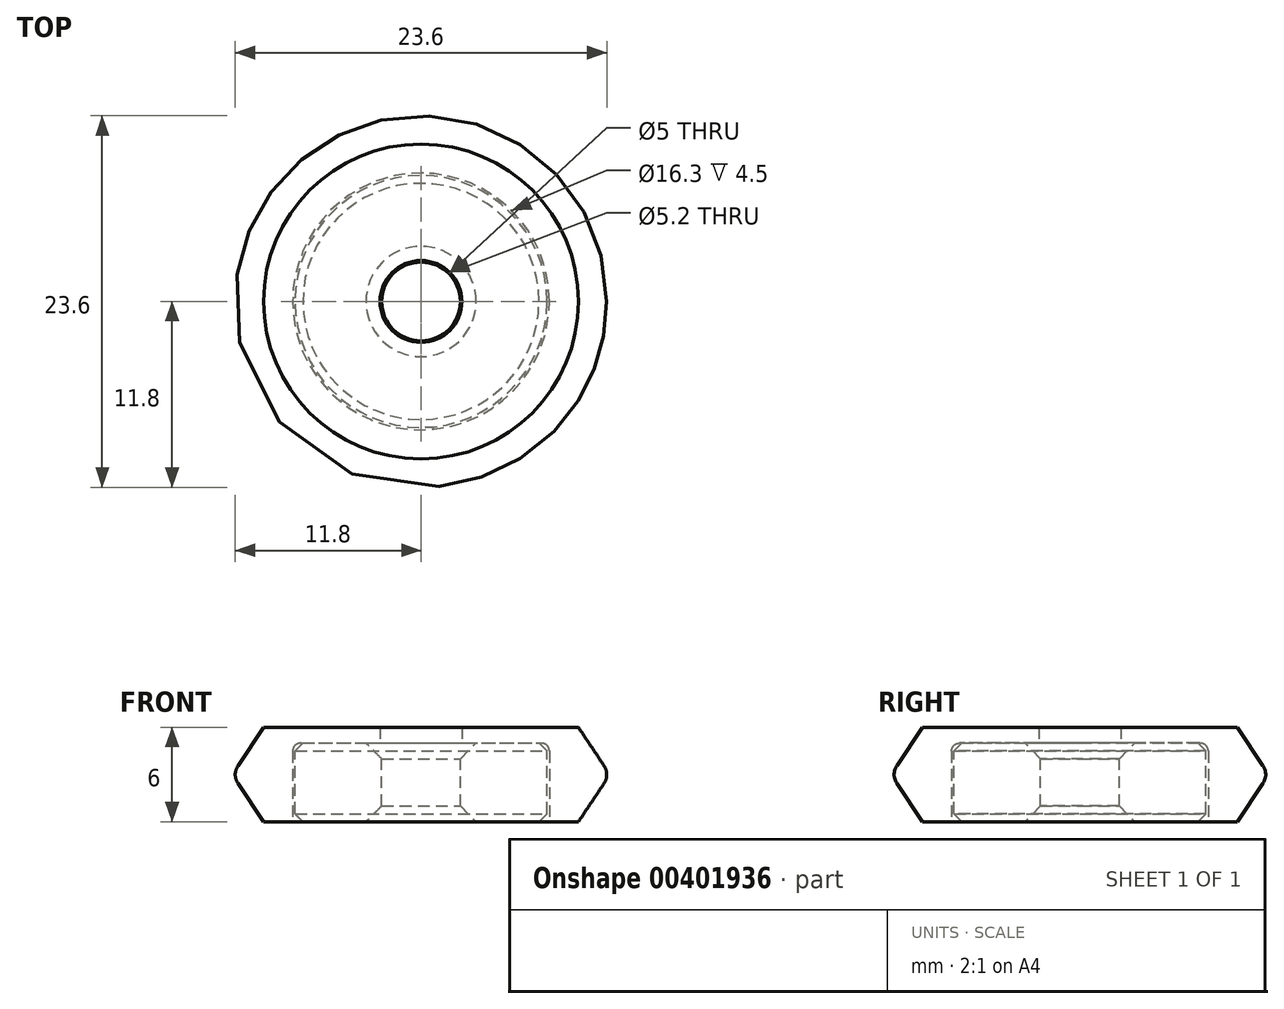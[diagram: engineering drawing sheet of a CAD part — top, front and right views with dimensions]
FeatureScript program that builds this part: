
annotation { "Feature Type Name" : "Feature", "Feature Type Description" : "" }
export const myFeature = defineFeature(function(context is Context, id is Id, definition is map)
    precondition{}
    {
        {
            var Q0;
            Q0=qCreatedBy(makeId("Top.planeOp"),FACE);
            var sketch = newSketch(context, id + "F0", { "sketchPlane" : qUnion([Q0])});
            skCircle(sketch, "E0", {"center": v(0, 0) * mm, "radius": 10 * mm});
            skSolve(sketch);
        }
        {
            var Q0;
            Q0=qCreatedBy(makeId("Top.planeOp"),FACE);
            cPlane(context, id + "F1", {"entities" : qUnion([Q0]), "cplaneType" : CPlaneType.OFFSET, "offset" : 3 * mm, "width" : 150 * mm, "height" : 150 * mm});
        }
        {
            var Q0;
            Q0=qCreatedBy(id+"F1.planeOp",FACE);
            var sketch = newSketch(context, id + "F2", { "sketchPlane" : qUnion([Q0])});
            skCircle(sketch, "E1", {"center": v(0, 0) * mm, "radius": 12 * mm});
            skSolve(sketch);
        }
        {
            var Q0;
            Q0=makeQuery(id+"F2.imprint","IMPRINT",FACE,{"disambiguationData":[TD([[makeQuery(id+"F2.imprint","IMPRINT",EDGE,{"derivedFrom":sQuery(id+"F2.wireOp",EDGE,"E1")}),1.0]])]});
            var Q1;
            Q1=makeQuery(id+"F0.imprint","IMPRINT",FACE,{"disambiguationData":[TD([[makeQuery(id+"F0.imprint","IMPRINT",EDGE,{"derivedFrom":sQuery(id+"F0.wireOp",EDGE,"E0")}),1.0]])]});
            loft(context, id + "F3", {"sheetProfilesArray" : [{ "sheetProfileEntities" : qUnion([Q0]) }, { "sheetProfileEntities" : qUnion([Q1]) }]});
        }
        {
            var Q0;
            Q0=makeQuery(id+"F3.opLoft","SWEPT_BODY",BODY,{"disambiguationData":[OSD([makeQuery(id+"F0.imprint","IMPRINT",FACE,{"disambiguationData":[TD([[makeQuery(id+"F0.imprint","IMPRINT",EDGE,{"derivedFrom":sQuery(id+"F0.wireOp",EDGE,"E0")}),1.0]])]}),makeQuery(id+"F2.imprint","IMPRINT",FACE,{"disambiguationData":[TD([[makeQuery(id+"F2.imprint","IMPRINT",EDGE,{"derivedFrom":sQuery(id+"F2.wireOp",EDGE,"E1")}),1.0]])]})])]});
            var Q1;
            Q1=qCreatedBy(id+"F1.planeOp",FACE);
            mirror(context, id + "F4", {"operationType" : NewBodyOperationType.ADD, "entities" : qUnion([Q0]), "mirrorPlane" : qUnion([Q1])});
        }
        {
            var Q0;
            Q0=makeQuery(id+"F3.opLoft","CAP_FACE",FACE,{"disambiguationData":[OSD([makeQuery(id+"F0.imprint","IMPRINT",FACE,{"disambiguationData":[TD([[makeQuery(id+"F0.imprint","IMPRINT",EDGE,{"derivedFrom":sQuery(id+"F0.wireOp",EDGE,"E0")}),1.0]])]})])],"isStart":true});
            var sketch = newSketch(context, id + "F5", { "sketchPlane" : qUnion([Q0])});
            skCircle(sketch, "E2", {"center": v(0, 0) * mm, "radius": 8.15 * mm});
            skSolve(sketch);
        }
        {
            var Q0;
            Q0=makeQuery(id+"F5.imprint","IMPRINT",FACE,{"disambiguationData":[TD([[makeQuery(id+"F5.imprint","IMPRINT",EDGE,{"derivedFrom":sQuery(id+"F5.wireOp",EDGE,"E2")}),1.0]])]});
            extrude(context, id + "F6", {"entities" : qUnion([Q0]), "operationType" : NewBodyOperationType.REMOVE, "oppositeDirection" : true, "depth" : 5 * mm});
        }
        {
            var Q0;
            Q0=makeQuery(id+"F6.boolean.opBoolean","COPY",FACE,{"derivedFrom":makeQuery(id+"F6.opExtrude","CAP_FACE",FACE,{"disambiguationData":[OSD([sQuery(id+"F5.wireOp",EDGE,"E2")])],"isStart":false})});
            var sketch = newSketch(context, id + "F7", { "sketchPlane" : qUnion([Q0])});
            skCircle(sketch, "E3", {"center": v(0, 0) * mm, "radius": 2.6 * mm});
            skSolve(sketch);
        }
        {
            var Q0;
            Q0=makeQuery(id+"F7.imprint","IMPRINT",FACE,{"disambiguationData":[TD([[makeQuery(id+"F7.imprint","IMPRINT",EDGE,{"derivedFrom":sQuery(id+"F7.wireOp",EDGE,"E3")}),1.0]])]});
            extrude(context, id + "F8", {"entities" : qUnion([Q0]), "operationType" : NewBodyOperationType.REMOVE, "endBound" : BoundingType.UP_TO_NEXT, "oppositeDirection" : true, "depth" : 25 * mm});
        }
        {
            var Q0;
            {var subQ0=makeQuery(id+"F3.opLoft","MID_CAP_EDGE",EDGE,{"disambiguationData":[OSD([sQuery(id+"F2.wireOp",EDGE,"E1")])],"capPos":0.0});Q0=makeQuery(id+"F4.boolean.opBoolean","MERGE",EDGE,{"derivedFrom":[subQ0,makeQuery(id+"F4.opPattern","COPY",EDGE,{"derivedFrom":subQ0,"instanceName":"1"})]});}
            fillet(context, id + "F9", {"entities" : qUnion([Q0]), "radius" : 1 * mm, "tangentPropagation" : true, "allowEdgeOverflow" : false});
        }
        {
            var Q0;
            Q0=makeQuery(id+"F6.boolean.opBoolean","COPY",EDGE,{"derivedFrom":makeQuery(id+"F6.opExtrude","CAP_EDGE",EDGE,{"disambiguationData":[OSD([sQuery(id+"F5.wireOp",EDGE,"E2")])],"isStart":false})});
            fillet(context, id + "F10", {"entities" : qUnion([Q0]), "radius" : 0.5 * mm, "tangentPropagation" : true, "allowEdgeOverflow" : false});
        }
        {
            var Q0;
            Q0=makeQuery(id+"F6.boolean.opBoolean","COPY",FACE,{"derivedFrom":makeQuery(id+"F6.opExtrude","CAP_FACE",FACE,{"disambiguationData":[OSD([sQuery(id+"F5.wireOp",EDGE,"E2")])],"isStart":false})});
            var sketch = newSketch(context, id + "F11", { "sketchPlane" : qUnion([Q0])});
            skCircle(sketch, "E4", {"center": v(0, 0) * mm, "radius": 8 * mm});
            skCircle(sketch, "E5", {"center": v(0, 0) * mm, "radius": 2.5 * mm});
            skSolve(sketch);
        }
        {
            var Q0;
            Q0 = qSketchRegion(id + "F11", true);
            extrude(context, id + "F12", {"entities" : qUnion([Q0]), "depth" : 5 * mm});
        }
        {
            var Q0;
            Q0=makeQuery(id+"F12.opExtrude","CAP_EDGE",EDGE,{"disambiguationData":[OSD([sQuery(id+"F11.wireOp",EDGE,"E4")])],"isStart":false});
            var Q1;
            Q1=makeQuery(id+"F12.opExtrude","CAP_EDGE",EDGE,{"disambiguationData":[OSD([sQuery(id+"F11.wireOp",EDGE,"E4")])],"isStart":true});
            chamfer(context, id + "F13", {"entities" : qUnion([Q0, Q1]), "width" : 0.5 * mm, "tangentPropagation" : true});
        }
        {
            var Q0;
            Q0=makeQuery(id+"F12.opExtrude","CAP_EDGE",EDGE,{"disambiguationData":[OSD([sQuery(id+"F11.wireOp",EDGE,"E5")])],"isStart":false});
            var Q1;
            Q1=makeQuery(id+"F12.opExtrude","CAP_EDGE",EDGE,{"disambiguationData":[OSD([sQuery(id+"F11.wireOp",EDGE,"E5")])],"isStart":true});
            chamfer(context, id + "F14", {"entities" : qUnion([Q0, Q1]), "width" : 1 * mm, "tangentPropagation" : true});
        }
    });
